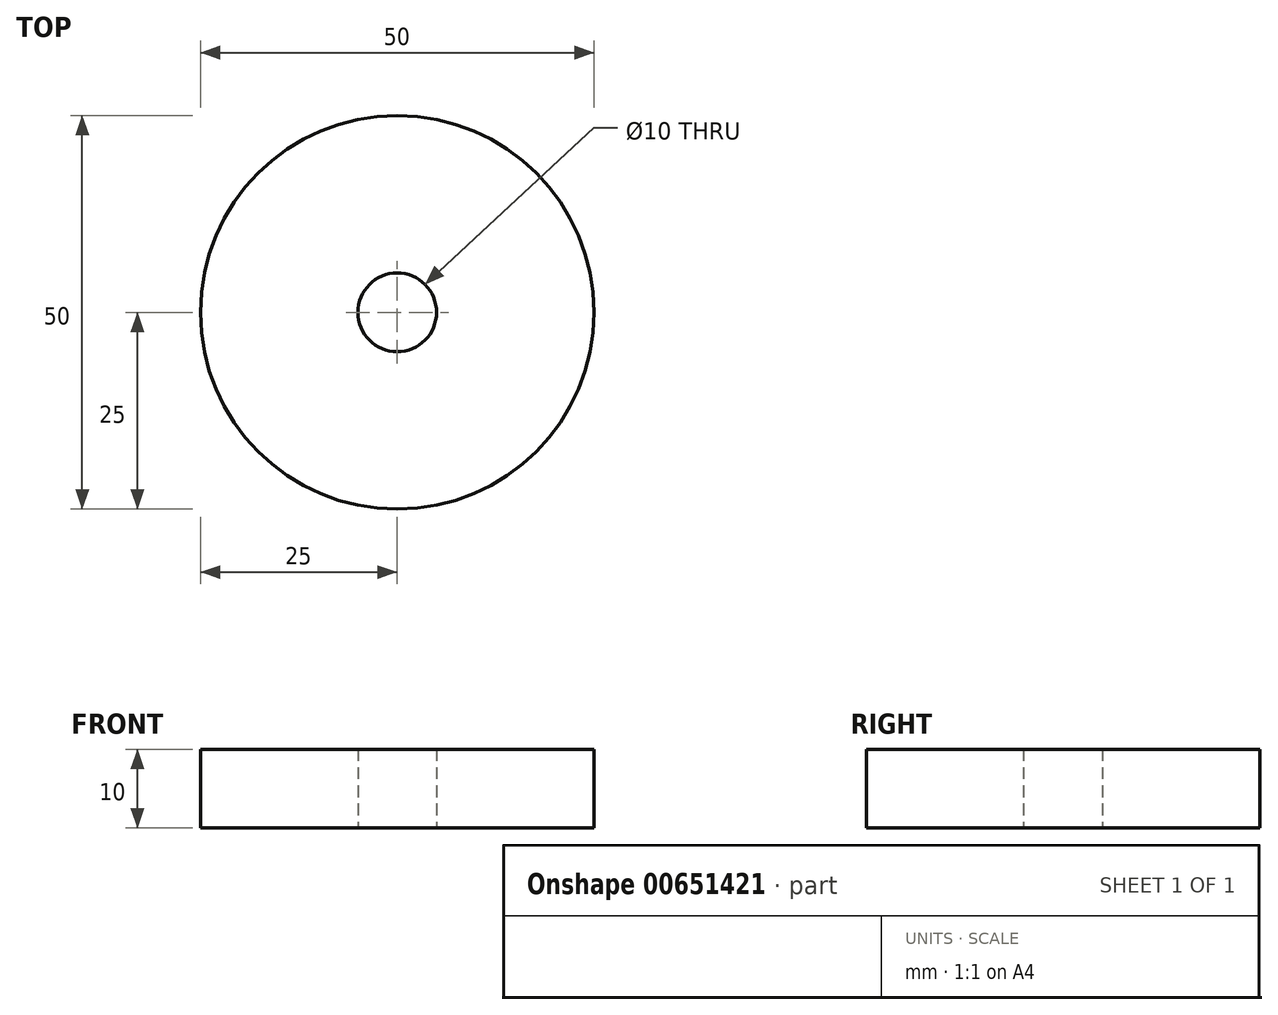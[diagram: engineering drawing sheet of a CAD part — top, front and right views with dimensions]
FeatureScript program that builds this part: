
annotation { "Feature Type Name" : "Feature", "Feature Type Description" : "" }
export const myFeature = defineFeature(function(context is Context, id is Id, definition is map)
    precondition{}
    {
        {
            var Q0;
            Q0=qCreatedBy(makeId("Top.planeOp"),FACE);
            var sketch = newSketch(context, id + "F0", { "sketchPlane" : qUnion([Q0])});
            skCircle(sketch, "E0", {"center": v(0, 0) * mm, "radius": 25 * mm});
            skSolve(sketch);
        }
        {
            var Q0;
            Q0=makeQuery(id+"F0.imprint","IMPRINT",FACE,{"disambiguationData":[TD([[makeQuery(id+"F0.imprint","IMPRINT",EDGE,{"derivedFrom":sQuery(id+"F0.wireOp",EDGE,"E0")}),1.0]])]});
            extrude(context, id + "F1", {"entities" : qUnion([Q0]), "depth" : 10 * mm, "offsetDistance" : 25.4 * mm});
        }
        {
            var Q0;
            Q0=sQuery(id+"F0.wireOp",VERTEX,"E0.center");
            var Q1;
            Q1=makeQuery(id+"F1.opExtrude","SWEPT_BODY",BODY,{"disambiguationData":[OSD([sQuery(id+"F0.wireOp",EDGE,"E0")])]});
            hole(context, id + "F2", {"style" : HoleStyle.SIMPLE, "endStyle" : HoleEndStyle.THROUGH, "oppositeDirection" : true, "holeDiameter" : 10 * mm, "majorDiameter" : 6.35 * mm, "isTappedThrough" : true, "tappedDepth" : 12.7 * mm, "tapClearance" : 3, "locations" : qUnion([Q0]), "scope" : qUnion([Q1])});
        }
    });
